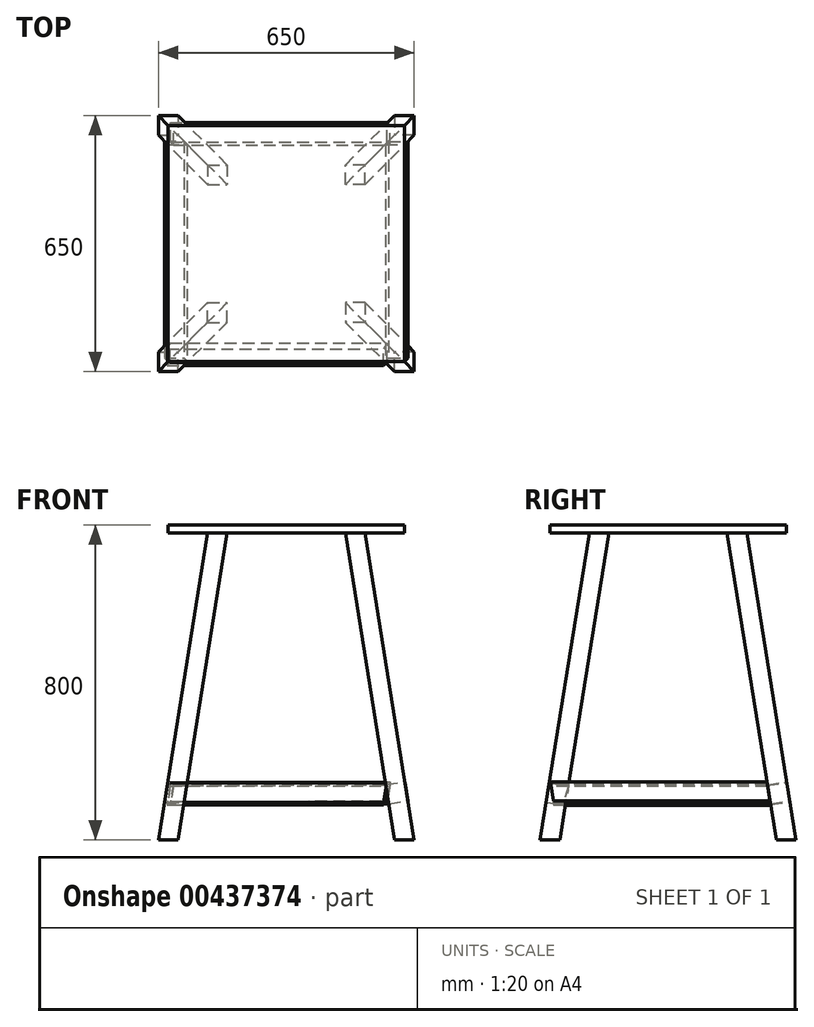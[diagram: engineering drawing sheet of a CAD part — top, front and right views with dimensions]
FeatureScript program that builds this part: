
annotation { "Feature Type Name" : "Feature", "Feature Type Description" : "" }
export const myFeature = defineFeature(function(context is Context, id is Id, definition is map)
    precondition{}
    {
        {
            var Q0;
            Q0=qCreatedBy(makeId("Top.planeOp"),FACE);
            var sketch = newSketch(context, id + "F0", { "sketchPlane" : qUnion([Q0])});
            skLineSegment(sketch, "E0.bottom", {"start": v(-300, 300) * mm, "end": v(300, 300) * mm});
            skLineSegment(sketch, "E0.top", {"start": v(-300, -300) * mm, "end": v(300, -300) * mm});
            skLineSegment(sketch, "E0.left", {"start": v(-300, 300) * mm, "end": v(-300, -300) * mm});
            skLineSegment(sketch, "E0.right", {"start": v(300, 300) * mm, "end": v(300, -300) * mm});
            skPoint(sketch, "E0.middle", {"position": v(0, 0) * mm});
            skSolve(sketch);
        }
        {
            var Q0;
            Q0 = qSketchRegion(id + "F0", true);
            extrude(context, id + "F1", {"entities" : qUnion([Q0]), "depth" : 20 * mm});
        }
        {
            var Q0;
            Q0=makeQuery(id+"F1.opExtrude","CAP_FACE",FACE,{"disambiguationData":[OSD([sQuery(id+"F0.wireOp",EDGE,"E0.bottom"),sQuery(id+"F0.wireOp",EDGE,"E0.top"),sQuery(id+"F0.wireOp",EDGE,"E0.left"),sQuery(id+"F0.wireOp",EDGE,"E0.right")])],"isStart":true});
            var sketch = newSketch(context, id + "F2", { "sketchPlane" : qUnion([Q0])});
            skLineSegment(sketch, "E1.bottom", {"start": v(-200, -200) * mm, "end": v(-150, -200) * mm});
            skLineSegment(sketch, "E1.top", {"start": v(-200, -150) * mm, "end": v(-150, -150) * mm});
            skLineSegment(sketch, "E1.left", {"start": v(-200, -200) * mm, "end": v(-200, -150) * mm});
            skLineSegment(sketch, "E1.right", {"start": v(-150, -200) * mm, "end": v(-150, -150) * mm});
            skLineSegment(sketch, "E2.MirrorCS", {"start": v(200, -200) * mm, "end": v(150, -200) * mm});
            skLineSegment(sketch, "E3.MirrorCS", {"start": v(200, -150) * mm, "end": v(200, -200) * mm});
            skLineSegment(sketch, "E4.MirrorCS", {"start": v(150, -150) * mm, "end": v(150, -200) * mm});
            skLineSegment(sketch, "E5.MirrorCS", {"start": v(200, -150) * mm, "end": v(150, -150) * mm});
            skLineSegment(sketch, "E6.MirrorCS", {"start": v(150, 150) * mm, "end": v(150, 200) * mm});
            skLineSegment(sketch, "E7.MirrorCS", {"start": v(200, 200) * mm, "end": v(150, 200) * mm});
            skLineSegment(sketch, "E8.MirrorCS", {"start": v(200, 150) * mm, "end": v(200, 200) * mm});
            skLineSegment(sketch, "E9.MirrorCS", {"start": v(200, 150) * mm, "end": v(150, 150) * mm});
            skLineSegment(sketch, "E10.MirrorCS", {"start": v(-150, 200) * mm, "end": v(-150, 150) * mm});
            skLineSegment(sketch, "E11.MirrorCS", {"start": v(-200, 200) * mm, "end": v(-200, 150) * mm});
            skLineSegment(sketch, "E12.MirrorCS", {"start": v(-200, 150) * mm, "end": v(-150, 150) * mm});
            skLineSegment(sketch, "E13.MirrorCS", {"start": v(-200, 200) * mm, "end": v(-150, 200) * mm});
            skSolve(sketch);
        }
        {
            var Q0;
            Q0=qCreatedBy(makeId("Top.planeOp"),FACE);
            cPlane(context, id + "F3", {"entities" : qUnion([Q0]), "cplaneType" : CPlaneType.OFFSET, "offset" : 780 * mm, "oppositeDirection" : true, "width" : 150 * mm, "height" : 150 * mm});
        }
        {
            var Q0;
            Q0=qCreatedBy(id+"F3.planeOp",FACE);
            var sketch = newSketch(context, id + "F4", { "sketchPlane" : qUnion([Q0])});
            skLineSegment(sketch, "E14.bottom", {"start": v(-325, 325) * mm, "end": v(-275, 325) * mm});
            skLineSegment(sketch, "E14.top", {"start": v(-325, 275) * mm, "end": v(-275, 275) * mm});
            skLineSegment(sketch, "E14.left", {"start": v(-325, 325) * mm, "end": v(-325, 275) * mm});
            skLineSegment(sketch, "E14.right", {"start": v(-275, 325) * mm, "end": v(-275, 275) * mm});
            skLineSegment(sketch, "E15.MirrorCS", {"start": v(325, 325) * mm, "end": v(275, 325) * mm});
            skLineSegment(sketch, "E16.MirrorCS", {"start": v(325, 325) * mm, "end": v(325, 275) * mm});
            skLineSegment(sketch, "E17.MirrorCS", {"start": v(325, 275) * mm, "end": v(275, 275) * mm});
            skLineSegment(sketch, "E18.MirrorCS", {"start": v(275, 325) * mm, "end": v(275, 275) * mm});
            skLineSegment(sketch, "E19.MirrorCS", {"start": v(-325, -325) * mm, "end": v(-275, -325) * mm});
            skLineSegment(sketch, "E20.MirrorCS", {"start": v(-325, -325) * mm, "end": v(-325, -275) * mm});
            skLineSegment(sketch, "E21.MirrorCS", {"start": v(-275, -325) * mm, "end": v(-275, -275) * mm});
            skLineSegment(sketch, "E22.MirrorCS", {"start": v(-325, -275) * mm, "end": v(-275, -275) * mm});
            skLineSegment(sketch, "E23.MirrorCS", {"start": v(325, -275) * mm, "end": v(275, -275) * mm});
            skLineSegment(sketch, "E24.MirrorCS", {"start": v(325, -325) * mm, "end": v(275, -325) * mm});
            skLineSegment(sketch, "E25.MirrorCS", {"start": v(275, -325) * mm, "end": v(275, -275) * mm});
            skLineSegment(sketch, "E26.MirrorCS", {"start": v(325, -325) * mm, "end": v(325, -275) * mm});
            skSolve(sketch);
        }
        {
            var Q1;
            Q1=makeQuery(id+"F2.imprint","IMPRINT",FACE,{"disambiguationData":[TD([[makeQuery(id+"F2.imprint","IMPRINT",EDGE,{"derivedFrom":sQuery(id+"F2.wireOp",EDGE,"E2.MirrorCS")}),-1.0]])]});
            var Q2;
            Q2=makeQuery(id+"F4.imprint","IMPRINT",FACE,{"disambiguationData":[TD([[makeQuery(id+"F4.imprint","IMPRINT",EDGE,{"derivedFrom":sQuery(id+"F4.wireOp",EDGE,"E15.MirrorCS")}),1.0]])]});
            loft(context, id + "F5", {"operationType" : NewBodyOperationType.ADD, "sheetProfilesArray" : [{ "sheetProfileEntities" : qUnion([Q1]) }, { "sheetProfileEntities" : qUnion([Q2]) }]});
        }
        {
            var Q1;
            Q1=makeQuery(id+"F2.imprint","IMPRINT",FACE,{"disambiguationData":[TD([[makeQuery(id+"F2.imprint","IMPRINT",EDGE,{"derivedFrom":sQuery(id+"F2.wireOp",EDGE,"E6.MirrorCS")}),-1.0]])]});
            var Q2;
            Q2=makeQuery(id+"F4.imprint","IMPRINT",FACE,{"disambiguationData":[TD([[makeQuery(id+"F4.imprint","IMPRINT",EDGE,{"derivedFrom":sQuery(id+"F4.wireOp",EDGE,"E23.MirrorCS")}),1.0]])]});
            loft(context, id + "F6", {"operationType" : NewBodyOperationType.ADD, "sheetProfilesArray" : [{ "sheetProfileEntities" : qUnion([Q1]) }, { "sheetProfileEntities" : qUnion([Q2]) }]});
        }
        {
            var Q1;
            Q1=makeQuery(id+"F2.imprint","IMPRINT",FACE,{"disambiguationData":[TD([[makeQuery(id+"F2.imprint","IMPRINT",EDGE,{"derivedFrom":sQuery(id+"F2.wireOp",EDGE,"E1.bottom")}),1.0]])]});
            var Q2;
            Q2=makeQuery(id+"F4.imprint","IMPRINT",FACE,{"disambiguationData":[TD([[makeQuery(id+"F4.imprint","IMPRINT",EDGE,{"derivedFrom":sQuery(id+"F4.wireOp",EDGE,"E14.bottom")}),-1.0]])]});
            loft(context, id + "F7", {"operationType" : NewBodyOperationType.ADD, "sheetProfilesArray" : [{ "sheetProfileEntities" : qUnion([Q1]) }, { "sheetProfileEntities" : qUnion([Q2]) }]});
        }
        {
            var Q1;
            Q1=makeQuery(id+"F2.imprint","IMPRINT",FACE,{"disambiguationData":[TD([[makeQuery(id+"F2.imprint","IMPRINT",EDGE,{"derivedFrom":sQuery(id+"F2.wireOp",EDGE,"E10.MirrorCS")}),-1.0]])]});
            var Q2;
            Q2=makeQuery(id+"F4.imprint","IMPRINT",FACE,{"disambiguationData":[TD([[makeQuery(id+"F4.imprint","IMPRINT",EDGE,{"derivedFrom":sQuery(id+"F4.wireOp",EDGE,"E19.MirrorCS")}),1.0]])]});
            loft(context, id + "F8", {"operationType" : NewBodyOperationType.ADD, "sheetProfilesArray" : [{ "sheetProfileEntities" : qUnion([Q1]) }, { "sheetProfileEntities" : qUnion([Q2]) }]});
        }
        {
            var Q0;
            Q0=makeQuery(id+"F5.opLoft","SWEPT_FACE",FACE,{"disambiguationData":[OSD([sQuery(id+"F2.wireOp",EDGE,"E3.MirrorCS"),sQuery(id+"F2.wireOp",EDGE,"E4.MirrorCS"),sQuery(id+"F2.wireOp",EDGE,"E5.MirrorCS"),sQuery(id+"F4.wireOp",EDGE,"E16.MirrorCS"),sQuery(id+"F4.wireOp",EDGE,"E17.MirrorCS"),sQuery(id+"F4.wireOp",EDGE,"E18.MirrorCS")])]});
            var sketch = newSketch(context, id + "F9", { "sketchPlane" : qUnion([Q0])});
            skLineSegment(sketch, "E27.bottom", {"start": v(259.18, -663.69) * mm, "end": v(309.18, -663.69) * mm});
            skLineSegment(sketch, "E27.top", {"start": v(259.18, -713.69) * mm, "end": v(309.18, -713.69) * mm});
            skLineSegment(sketch, "E27.left", {"start": v(259.18, -663.69) * mm, "end": v(259.18, -713.69) * mm});
            skLineSegment(sketch, "E27.right", {"start": v(309.18, -663.69) * mm, "end": v(309.18, -713.69) * mm});
            skSolve(sketch);
        }
        {
            var Q0;
            Q0=makeQuery(id+"F5.opLoft","SWEPT_FACE",FACE,{"disambiguationData":[OSD([sQuery(id+"F2.wireOp",EDGE,"E2.MirrorCS"),sQuery(id+"F2.wireOp",EDGE,"E4.MirrorCS"),sQuery(id+"F2.wireOp",EDGE,"E5.MirrorCS"),sQuery(id+"F4.wireOp",EDGE,"E15.MirrorCS"),sQuery(id+"F4.wireOp",EDGE,"E17.MirrorCS"),sQuery(id+"F4.wireOp",EDGE,"E18.MirrorCS")])]});
            var sketch = newSketch(context, id + "F10", { "sketchPlane" : qUnion([Q0])});
            skLineSegment(sketch, "E28", {"start": v(-229.42, -525.62) * mm, "end": v(320.58, -525.62) * mm});
            skSolve(sketch);
        }
        {
            var Q0;
            Q0 = qSketchRegion(id + "F9", true);
            var Q1;
            Q1=sQuery(id+"F10.wireOp",EDGE,"E28");
            sweep(context, id + "F11", {"profiles" : qUnion([Q0]), "path" : qUnion([Q1])});
        }
        {
            var Q0;
            Q0=makeQuery(id+"F11.opSweep","SWEPT_BODY",BODY,{"disambiguationData":[OSD([sQuery(id+"F9.wireOp",EDGE,"E27.bottom"),sQuery(id+"F9.wireOp",EDGE,"E27.top"),sQuery(id+"F9.wireOp",EDGE,"E27.left"),sQuery(id+"F9.wireOp",EDGE,"E27.right"),sQuery(id+"F10.wireOp",EDGE,"E28")])]});
            var Q1;
            Q1=makeQuery(id+"F11.opSweep","SWEPT_EDGE",EDGE,{"disambiguationData":[OSD([sQuery(id+"F2.wireOp",EDGE,"E3.MirrorCS"),sQuery(id+"F2.wireOp",EDGE,"E5.MirrorCS"),sQuery(id+"F4.wireOp",EDGE,"E16.MirrorCS"),sQuery(id+"F4.wireOp",EDGE,"E17.MirrorCS"),sQuery(id+"F9.wireOp",EDGE,"E27.top"),sQuery(id+"F9.wireOp",EDGE,"E27.right"),sQuery(id+"F10.wireOp",EDGE,"E28")])]});
            transform(context, id + "F12", {"entities" : qUnion([Q0]), "transformType" : TransformType.ROTATION, "transformAxis" : qUnion([Q1]), "angle" : 8.2 * degree, "makeCopy" : false});
        }
        {
            var Q0;
            Q0=makeQuery(id+"F11.opSweep","SWEPT_BODY",BODY,{"disambiguationData":[OSD([sQuery(id+"F9.wireOp",EDGE,"E27.bottom"),sQuery(id+"F9.wireOp",EDGE,"E27.top"),sQuery(id+"F9.wireOp",EDGE,"E27.left"),sQuery(id+"F9.wireOp",EDGE,"E27.right"),sQuery(id+"F10.wireOp",EDGE,"E28")])]});
            transform(context, id + "F13", {"entities" : qUnion([Q0]), "transformType" : TransformType.TRANSLATION_3D, "dx" : 0 * mm, "dy" : 537 * mm, "dz" : 16 * mm, "makeCopy" : true});
        }
        {
            var Q0;
            Q0=makeQuery(id+"F13.opPattern","COPY",BODY,{"derivedFrom":makeQuery(id+"F11.opSweep","SWEPT_BODY",BODY,{"disambiguationData":[OSD([sQuery(id+"F9.wireOp",EDGE,"E27.bottom"),sQuery(id+"F9.wireOp",EDGE,"E27.top"),sQuery(id+"F9.wireOp",EDGE,"E27.left"),sQuery(id+"F9.wireOp",EDGE,"E27.right"),sQuery(id+"F10.wireOp",EDGE,"E28")])]}),"instanceName":"1"});
            var Q1;
            Q1=makeQuery(id+"F13.opPattern","COPY",EDGE,{"derivedFrom":makeQuery(id+"F11.opSweep","CAP_EDGE",EDGE,{"disambiguationData":[OSD([sQuery(id+"F9.wireOp",EDGE,"E27.left"),sQuery(id+"F10.wireOp",VERTEX,"E28.end")])],"isStart":false}),"instanceName":"1"});
            transform(context, id + "F14", {"entities" : qUnion([Q0]), "transformType" : TransformType.ROTATION, "transformAxis" : qUnion([Q1]), "angle" : 90 * degree, "oppositeDirection" : true, "makeCopy" : false});
        }
        {
            var Q0;
            Q0=makeQuery(id+"F13.opPattern","COPY",BODY,{"derivedFrom":makeQuery(id+"F11.opSweep","SWEPT_BODY",BODY,{"disambiguationData":[OSD([sQuery(id+"F9.wireOp",EDGE,"E27.bottom"),sQuery(id+"F9.wireOp",EDGE,"E27.top"),sQuery(id+"F9.wireOp",EDGE,"E27.left"),sQuery(id+"F9.wireOp",EDGE,"E27.right"),sQuery(id+"F10.wireOp",EDGE,"E28")])]}),"instanceName":"1"});
            var Q1;
            Q1=makeQuery(id+"F13.opPattern","COPY",EDGE,{"derivedFrom":makeQuery(id+"F11.opSweep","CAP_EDGE",EDGE,{"disambiguationData":[OSD([sQuery(id+"F9.wireOp",EDGE,"E27.top"),sQuery(id+"F10.wireOp",VERTEX,"E28.end")])],"isStart":false}),"instanceName":"1"});
            transform(context, id + "F15", {"entities" : qUnion([Q0]), "transformType" : TransformType.ROTATION, "transformAxis" : qUnion([Q1]), "angle" : 15 * degree, "makeCopy" : false});
        }
        {
            var Q0;
            Q0=makeQuery(id+"F13.opPattern","COPY",BODY,{"derivedFrom":makeQuery(id+"F11.opSweep","SWEPT_BODY",BODY,{"disambiguationData":[OSD([sQuery(id+"F9.wireOp",EDGE,"E27.bottom"),sQuery(id+"F9.wireOp",EDGE,"E27.top"),sQuery(id+"F9.wireOp",EDGE,"E27.left"),sQuery(id+"F9.wireOp",EDGE,"E27.right"),sQuery(id+"F10.wireOp",EDGE,"E28")])]}),"instanceName":"1"});
            var Q1;
            Q1=sQuery(id+"F4.wireOp",EDGE,"E18.MirrorCS");
            transform(context, id + "F16", {"entities" : qUnion([Q0]), "transformType" : TransformType.TRANSLATION_ENTITY, "oppositeDirectionEntity" : false, "transformLine" : qUnion([Q1]), "makeCopy" : false});
        }
        {
            var Q0;
            Q0=makeQuery(id+"F13.opPattern","COPY",BODY,{"derivedFrom":makeQuery(id+"F11.opSweep","SWEPT_BODY",BODY,{"disambiguationData":[OSD([sQuery(id+"F9.wireOp",EDGE,"E27.bottom"),sQuery(id+"F9.wireOp",EDGE,"E27.top"),sQuery(id+"F9.wireOp",EDGE,"E27.left"),sQuery(id+"F9.wireOp",EDGE,"E27.right"),sQuery(id+"F10.wireOp",EDGE,"E28")])]}),"instanceName":"1"});
            var Q1;
            Q1=makeQuery(id+"F5.opLoft","SWEPT_EDGE",EDGE,{"disambiguationData":[OSD([sQuery(id+"F2.wireOp",EDGE,"E2.MirrorCS"),sQuery(id+"F2.wireOp",EDGE,"E4.MirrorCS"),sQuery(id+"F4.wireOp",EDGE,"E15.MirrorCS"),sQuery(id+"F4.wireOp",EDGE,"E18.MirrorCS")])]});
            transform(context, id + "F17", {"entities" : qUnion([Q0]), "transformType" : TransformType.ROTATION, "transformAxis" : qUnion([Q1]), "angle" : 1.3 * degree, "makeCopy" : false});
        }
        {
            var Q0;
            Q0=makeQuery(id+"F8.opLoft","SWEPT_FACE",FACE,{"disambiguationData":[OSD([sQuery(id+"F2.wireOp",EDGE,"E10.MirrorCS"),sQuery(id+"F2.wireOp",EDGE,"E11.MirrorCS"),sQuery(id+"F2.wireOp",EDGE,"E13.MirrorCS"),sQuery(id+"F4.wireOp",EDGE,"E19.MirrorCS"),sQuery(id+"F4.wireOp",EDGE,"E20.MirrorCS"),sQuery(id+"F4.wireOp",EDGE,"E21.MirrorCS")])]});
            var sketch = newSketch(context, id + "F18", { "sketchPlane" : qUnion([Q0])});
            skLineSegment(sketch, "E29", {"start": v(-274.2, -545.63) * mm, "end": v(275.8, -545.63) * mm});
            skSolve(sketch);
        }
        {
            var Q0;
            Q0=makeQuery(id+"F8.opLoft","SWEPT_FACE",FACE,{"disambiguationData":[OSD([sQuery(id+"F2.wireOp",EDGE,"E10.MirrorCS"),sQuery(id+"F2.wireOp",EDGE,"E12.MirrorCS"),sQuery(id+"F2.wireOp",EDGE,"E13.MirrorCS"),sQuery(id+"F4.wireOp",EDGE,"E19.MirrorCS"),sQuery(id+"F4.wireOp",EDGE,"E21.MirrorCS"),sQuery(id+"F4.wireOp",EDGE,"E22.MirrorCS")])]});
            var sketch = newSketch(context, id + "F19", { "sketchPlane" : qUnion([Q0])});
            skLineSegment(sketch, "E30.bottom", {"start": v(-301.9, -667.64) * mm, "end": v(-251.9, -667.64) * mm});
            skLineSegment(sketch, "E30.top", {"start": v(-301.9, -717.64) * mm, "end": v(-251.9, -717.64) * mm});
            skLineSegment(sketch, "E30.left", {"start": v(-301.9, -667.64) * mm, "end": v(-301.9, -717.64) * mm});
            skLineSegment(sketch, "E30.right", {"start": v(-251.9, -667.64) * mm, "end": v(-251.9, -717.64) * mm});
            skSolve(sketch);
        }
        {
            var Q0;
            {var subQ0=sQuery(id+"F19.wireOp",EDGE,"E30.bottom");Q0=makeQuery(id+"F19.imprint","IMPRINT",FACE,{"disambiguationData":[TD([[makeQuery(id+"F19.imprint","IMPRINT",EDGE,{"derivedFrom":subQ0}),-1.0]])]});}
            var Q1;
            Q1=sQuery(id+"F18.wireOp",EDGE,"E29");
            sweep(context, id + "F20", {"profiles" : qUnion([Q0]), "path" : qUnion([Q1])});
        }
        {
            var Q0;
            Q0=makeQuery(id+"F20.opSweep","SWEPT_BODY",BODY,{"disambiguationData":[OSD([sQuery(id+"F2.wireOp",EDGE,"E10.MirrorCS"),sQuery(id+"F2.wireOp",EDGE,"E12.MirrorCS"),sQuery(id+"F4.wireOp",EDGE,"E21.MirrorCS"),sQuery(id+"F4.wireOp",EDGE,"E22.MirrorCS"),sQuery(id+"F18.wireOp",EDGE,"E29"),sQuery(id+"F19.wireOp",EDGE,"E30.bottom"),sQuery(id+"F19.wireOp",EDGE,"E30.top"),sQuery(id+"F19.wireOp",EDGE,"E30.left")])]});
            var Q1;
            Q1=makeQuery(id+"F20.opSweep","SWEPT_EDGE",EDGE,{"disambiguationData":[OSD([sQuery(id+"F2.wireOp",EDGE,"E10.MirrorCS"),sQuery(id+"F2.wireOp",EDGE,"E13.MirrorCS"),sQuery(id+"F4.wireOp",EDGE,"E19.MirrorCS"),sQuery(id+"F4.wireOp",EDGE,"E21.MirrorCS"),sQuery(id+"F18.wireOp",EDGE,"E29"),sQuery(id+"F19.wireOp",EDGE,"E30.bottom"),sQuery(id+"F19.wireOp",EDGE,"E30.left")])]});
            transform(context, id + "F21", {"entities" : qUnion([Q0]), "transformType" : TransformType.ROTATION, "transformAxis" : qUnion([Q1]), "angle" : 8.8 * degree, "oppositeDirection" : true, "makeCopy" : false});
        }
        {
            var Q0;
            Q0=makeQuery(id+"F7.opLoft","SWEPT_FACE",FACE,{"disambiguationData":[OSD([sQuery(id+"F2.wireOp",EDGE,"E1.bottom"),sQuery(id+"F2.wireOp",EDGE,"E1.left"),sQuery(id+"F2.wireOp",EDGE,"E1.top"),sQuery(id+"F4.wireOp",EDGE,"E14.bottom"),sQuery(id+"F4.wireOp",EDGE,"E14.top"),sQuery(id+"F4.wireOp",EDGE,"E14.left")])]});
            var sketch = newSketch(context, id + "F22", { "sketchPlane" : qUnion([Q0])});
            skLineSegment(sketch, "E31", {"start": v(-233.23, -557.65) * mm, "end": v(316.77, -557.65) * mm});
            skSolve(sketch);
        }
        {
            var Q0;
            Q0=makeQuery(id+"F7.opLoft","SWEPT_FACE",FACE,{"disambiguationData":[OSD([sQuery(id+"F2.wireOp",EDGE,"E1.right"),sQuery(id+"F2.wireOp",EDGE,"E1.left"),sQuery(id+"F2.wireOp",EDGE,"E1.top"),sQuery(id+"F4.wireOp",EDGE,"E14.top"),sQuery(id+"F4.wireOp",EDGE,"E14.left"),sQuery(id+"F4.wireOp",EDGE,"E14.right")])]});
            var sketch = newSketch(context, id + "F23", { "sketchPlane" : qUnion([Q0])});
            skLineSegment(sketch, "E32.bottom", {"start": v(-301.9, -667.64) * mm, "end": v(-251.9, -667.64) * mm});
            skLineSegment(sketch, "E32.top", {"start": v(-301.9, -717.64) * mm, "end": v(-251.9, -717.64) * mm});
            skLineSegment(sketch, "E32.left", {"start": v(-301.9, -667.64) * mm, "end": v(-301.9, -717.64) * mm});
            skLineSegment(sketch, "E32.right", {"start": v(-251.9, -667.64) * mm, "end": v(-251.9, -717.64) * mm});
            skSolve(sketch);
        }
        {
            var Q0;
            Q0 = qSketchRegion(id + "F23", true);
            var Q1;
            Q1 = qConstructionFilter(qBodyType(qCreatedBy(id + "F22" ,EDGE), BodyType.WIRE), ConstructionObject.NO);
            sweep(context, id + "F24", {"profiles" : qUnion([Q0]), "path" : qUnion([Q1])});
        }
        {
            var Q0;
            Q0=makeQuery(id+"F24.opSweep","SWEPT_BODY",BODY,{"disambiguationData":[OSD([sQuery(id+"F22.wireOp",EDGE,"E31"),sQuery(id+"F23.wireOp",EDGE,"E32.bottom"),sQuery(id+"F23.wireOp",EDGE,"E32.top"),sQuery(id+"F23.wireOp",EDGE,"E32.left"),sQuery(id+"F23.wireOp",EDGE,"E32.right")])]});
            var Q1;
            Q1=makeQuery(id+"F24.opSweep","SWEPT_EDGE",EDGE,{"disambiguationData":[OSD([sQuery(id+"F2.wireOp",EDGE,"E1.left"),sQuery(id+"F2.wireOp",EDGE,"E1.top"),sQuery(id+"F4.wireOp",EDGE,"E14.top"),sQuery(id+"F4.wireOp",EDGE,"E14.left"),sQuery(id+"F22.wireOp",EDGE,"E31"),sQuery(id+"F23.wireOp",EDGE,"E32.bottom"),sQuery(id+"F23.wireOp",EDGE,"E32.left")])]});
            transform(context, id + "F25", {"entities" : qUnion([Q0]), "transformType" : TransformType.ROTATION, "transformAxis" : qUnion([Q1]), "angle" : 9 * degree, "oppositeDirection" : true, "makeCopy" : false});
        }
        {
            var Q0;
            Q0=makeQuery(id+"F13.opPattern","COPY",BODY,{"derivedFrom":makeQuery(id+"F11.opSweep","SWEPT_BODY",BODY,{"disambiguationData":[OSD([sQuery(id+"F9.wireOp",EDGE,"E27.bottom"),sQuery(id+"F9.wireOp",EDGE,"E27.top"),sQuery(id+"F9.wireOp",EDGE,"E27.left"),sQuery(id+"F9.wireOp",EDGE,"E27.right"),sQuery(id+"F10.wireOp",EDGE,"E28")])]}),"instanceName":"1"});
            transform(context, id + "F26", {"entities" : qUnion([Q0]), "transformType" : TransformType.TRANSLATION_3D, "dx" : 0 * mm, "dy" : 62 * mm, "dz" : 0 * mm, "makeCopy" : false});
        }
        {
            var Q0;
            Q0=makeQuery(id+"F13.opPattern","COPY",BODY,{"derivedFrom":makeQuery(id+"F11.opSweep","SWEPT_BODY",BODY,{"disambiguationData":[OSD([sQuery(id+"F9.wireOp",EDGE,"E27.bottom"),sQuery(id+"F9.wireOp",EDGE,"E27.top"),sQuery(id+"F9.wireOp",EDGE,"E27.left"),sQuery(id+"F9.wireOp",EDGE,"E27.right"),sQuery(id+"F10.wireOp",EDGE,"E28")])]}),"instanceName":"1"});
            transform(context, id + "F27", {"entities" : qUnion([Q0]), "transformType" : TransformType.TRANSLATION_3D, "dx" : 0 * mm, "dy" : 0 * mm, "dz" : -16 * mm, "makeCopy" : false});
        }
        {
            var Q0;
            Q0=makeQuery(id+"F13.opPattern","COPY",BODY,{"derivedFrom":makeQuery(id+"F11.opSweep","SWEPT_BODY",BODY,{"disambiguationData":[OSD([sQuery(id+"F9.wireOp",EDGE,"E27.bottom"),sQuery(id+"F9.wireOp",EDGE,"E27.top"),sQuery(id+"F9.wireOp",EDGE,"E27.left"),sQuery(id+"F9.wireOp",EDGE,"E27.right"),sQuery(id+"F10.wireOp",EDGE,"E28")])]}),"instanceName":"1"});
            var Q1;
            Q1=makeQuery(id+"F13.opPattern","COPY",EDGE,{"derivedFrom":makeQuery(id+"F11.opSweep","SWEPT_EDGE",EDGE,{"disambiguationData":[OSD([sQuery(id+"F2.wireOp",EDGE,"E4.MirrorCS"),sQuery(id+"F2.wireOp",EDGE,"E5.MirrorCS"),sQuery(id+"F4.wireOp",EDGE,"E17.MirrorCS"),sQuery(id+"F4.wireOp",EDGE,"E18.MirrorCS"),sQuery(id+"F9.wireOp",EDGE,"E27.top"),sQuery(id+"F9.wireOp",EDGE,"E27.left"),sQuery(id+"F10.wireOp",EDGE,"E28")])]}),"instanceName":"1"});
            transform(context, id + "F28", {"entities" : qUnion([Q0]), "transformType" : TransformType.ROTATION, "transformAxis" : qUnion([Q1]), "angle" : 0 * degree, "makeCopy" : false});
        }
        {
            var Q0;
            Q0=makeQuery(id+"F13.opPattern","COPY",FACE,{"derivedFrom":makeQuery(id+"F11.opSweep","SWEPT_FACE",FACE,{"disambiguationData":[OSD([sQuery(id+"F9.wireOp",EDGE,"E27.bottom"),sQuery(id+"F10.wireOp",EDGE,"E28")])]}),"instanceName":"1"});
            var sketch = newSketch(context, id + "F29", { "sketchPlane" : qUnion([Q0])});
            skLineSegment(sketch, "E33", {"start": v(226.53, 194.5) * mm, "end": v(226.54, 144.5) * mm});
            skSolve(sketch);
        }
        {
            var Q0;
            Q0=makeQuery(id+"F13.opPattern","COPY",BODY,{"derivedFrom":makeQuery(id+"F11.opSweep","SWEPT_BODY",BODY,{"disambiguationData":[OSD([sQuery(id+"F9.wireOp",EDGE,"E27.bottom"),sQuery(id+"F9.wireOp",EDGE,"E27.top"),sQuery(id+"F9.wireOp",EDGE,"E27.left"),sQuery(id+"F9.wireOp",EDGE,"E27.right"),sQuery(id+"F10.wireOp",EDGE,"E28")])]}),"instanceName":"1"});
            var Q1;
            Q1=sQuery(id+"F29.wireOp",EDGE,"E33");
            transform(context, id + "F30", {"entities" : qUnion([Q0]), "transformType" : TransformType.ROTATION, "transformAxis" : qUnion([Q1]), "angle" : 2 * degree, "oppositeDirection" : true, "makeCopy" : false});
        }
    });
